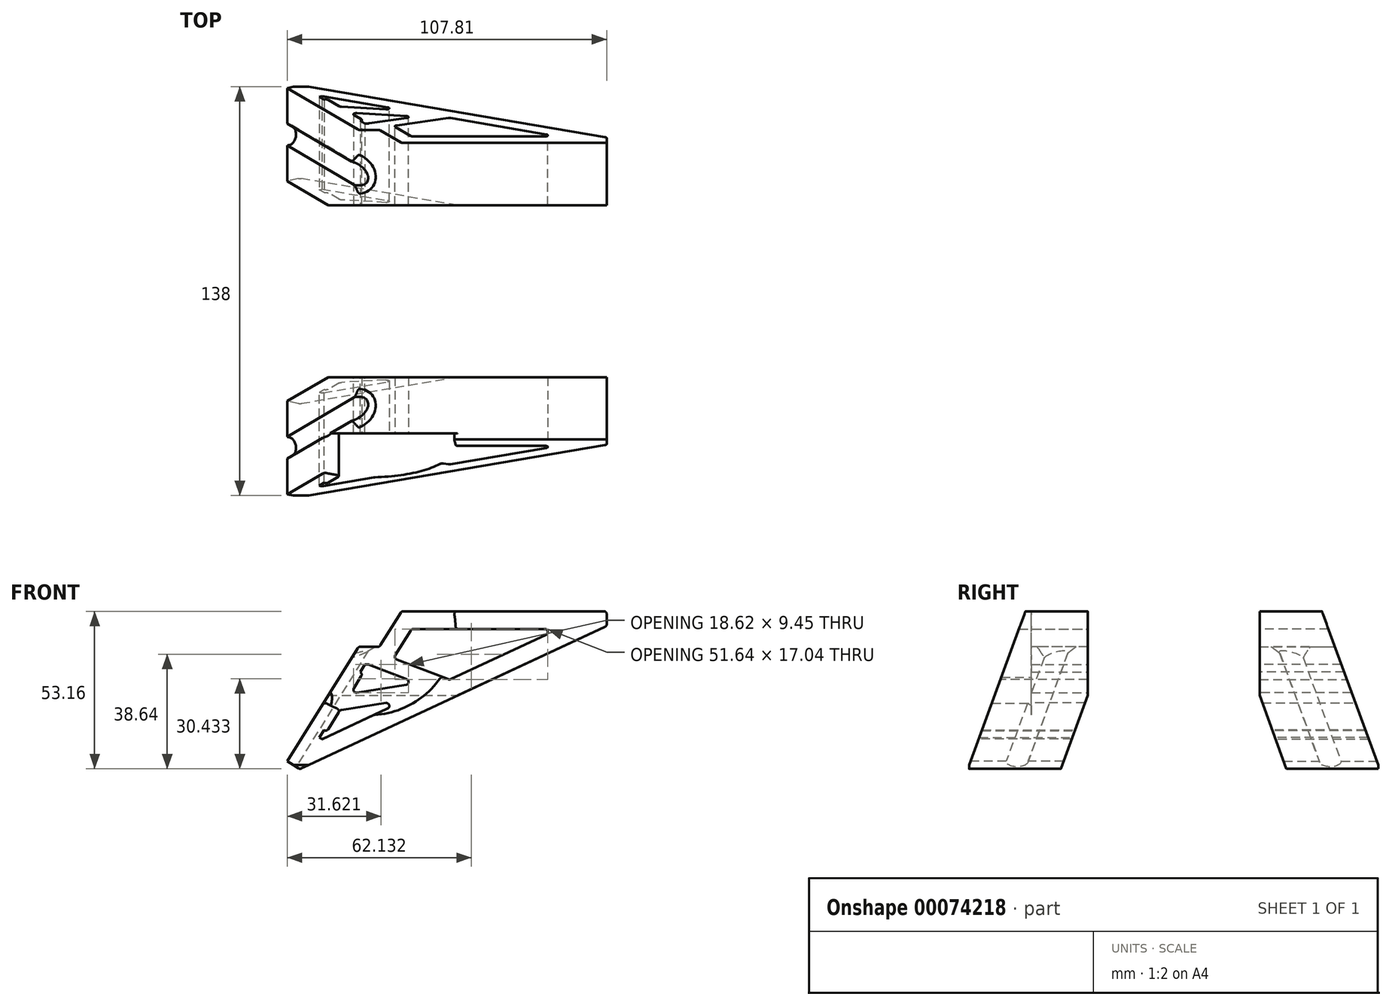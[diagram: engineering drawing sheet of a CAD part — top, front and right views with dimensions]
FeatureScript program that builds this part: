
annotation { "Feature Type Name" : "Feature", "Feature Type Description" : "" }
export const myFeature = defineFeature(function(context is Context, id is Id, definition is map)
    precondition{}
    {
        {
            var Q0;
            Q0=qCreatedBy(makeId("Front.planeOp"),FACE);
            cPlane(context, id + "F0", {"entities" : qUnion([Q0]), "cplaneType" : CPlaneType.OFFSET, "offset" : 88 * mm, "width" : 150 * mm, "height" : 150 * mm});
        }
        {
            var Q0;
            Q0=qCreatedBy(makeId("Front.planeOp"),FACE);
            var sketch = newSketch(context, id + "F1", { "sketchPlane" : qUnion([Q0])});
            skLineSegment(sketch, "E0", {"start": v(0, 0) * mm, "end": v(-100, 0) * mm});
            skLineSegment(sketch, "E1", {"start": v(-100, 0) * mm, "end": v(-151.66, -24.09) * mm});
            skLineSegment(sketch, "E2", {"start": v(-151.66, -24.09) * mm, "end": v(-166.46, -47.86) * mm});
            skSolve(sketch);
        }
        {
            var Q0;
            Q0=qCreatedBy(makeId("Right.planeOp"),FACE);
            var sketch = newSketch(context, id + "F2", { "sketchPlane" : qUnion([Q0])});
            skCircle(sketch, "E3", {"center": v(-4, 0) * mm, "radius": 4 * mm});
            skCircle(sketch, "E4", {"center": v(-84, 0) * mm, "radius": 4 * mm});
            skSolve(sketch);
        }
        {
            var Q0;
            Q0=qSketchRegion(id+"F2",true);
            var Q1;
            Q1=qConstructionFilter(qBodyType(qCreatedBy(id+"F1",EDGE),BodyType.WIRE),ConstructionObject.NO);
            sweep(context, id + "F3", {"profiles" : qUnion([Q0]), "path" : qUnion([Q1])});
        }
        {
            var Q0;
            Q0=qCreatedBy(makeId("Front.planeOp"),FACE);
            var Q1;
            Q1=qCreatedBy(id+"F0.planeOp",FACE);
            cPlane(context, id + "F4", {"entities" : qUnion([Q0, Q1]), "cplaneType" : CPlaneType.MID_PLANE, "offset" : 150 * mm, "width" : 150 * mm, "height" : 150 * mm});
        }
        {
            var Q0;
            Q0=qCreatedBy(id+"F4.planeOp",FACE);
            var sketch = newSketch(context, id + "F5", { "sketchPlane" : qUnion([Q0])});
            skCircle(sketch, "E5", {"center": v(0, 0) * mm, "radius": 5 * mm});
            skSolve(sketch);
        }
        {
            var Q0;
            Q0=makeQuery(id+"F3.opSweep","SWEPT_FACE",FACE,{"disambiguationData":[OSD([sQuery(id+"F1.wireOp",EDGE,"E2"),sQuery(id+"F2.wireOp",EDGE,"E3")])]});
            cPlane(context, id + "F6", {"entities" : qUnion([Q0]), "cplaneType" : CPlaneType.LINE_ANGLE, "offset" : 150 * mm, "angle" : 0 * degree, "width" : 150 * mm, "height" : 150 * mm});
        }
        {
            var Q0;
            Q0=qCreatedBy(id+"F6.planeOp",FACE);
            var Q1;
            Q1=sQuery(id+"F1.wireOp",VERTEX,"E0.start");
            cPlane(context, id + "F7", {"entities" : qUnion([Q0, Q1]), "cplaneType" : CPlaneType.PLANE_POINT, "offset" : 150 * mm, "width" : 150 * mm, "height" : 150 * mm});
        }
        {
            var Q0;
            Q0=qCreatedBy(id+"F7.planeOp",FACE);
            var sketch = newSketch(context, id + "F8", { "sketchPlane" : qUnion([Q0])});
            skLineSegment(sketch, "E6", {"start": v(80.5, 0) * mm, "end": v(119, -124) * mm});
            skLineSegment(sketch, "E7", {"start": v(119, -124) * mm, "end": v(119, -194) * mm});
            skLineSegment(sketch, "E8", {"start": v(80.5, 0) * mm, "end": v(44, 0) * mm});
            skSolve(sketch);
        }
        {
            var Q0;
            Q0=qCreatedBy(id+"F4.planeOp",FACE);
            var sketch = newSketch(context, id + "F9", { "sketchPlane" : qUnion([Q0])});
            skCircle(sketch, "E9", {"center": v(0, 0) * mm, "radius": 3.5 * mm});
            skSolve(sketch);
        }
        {
            var Q0;
            Q0=qSketchRegion(id+"F9",true);
            var Q1;
            Q1=qConstructionFilter(qBodyType(qCreatedBy(id+"F8",EDGE),BodyType.WIRE),ConstructionObject.NO);
            sweep(context, id + "F10", {"operationType" : NewBodyOperationType.ADD, "profiles" : qUnion([Q0]), "path" : qUnion([Q1])});
        }
        {
            var Q0;
            Q0=makeQuery(id+"F3.opSweep","SWEPT_BODY",BODY,{"disambiguationData":[OSD([sQuery(id+"F1.wireOp",EDGE,"E2"),sQuery(id+"F2.wireOp",EDGE,"E4")])]});
            var Q1;
            Q1=qCreatedBy(id+"F4.planeOp",FACE);
            mirror(context, id + "F11", {"operationType" : NewBodyOperationType.ADD, "entities" : qUnion([Q0]), "mirrorPlane" : qUnion([Q1])});
        }
        {
            var Q0;
            Q0=qSketchRegion(id+"F5",true);
            extrude(context, id + "F12", {"entities" : qUnion([Q0]), "operationType" : NewBodyOperationType.ADD, "depth" : 50 * mm, "hasSecondDirection" : true, "secondDirectionOppositeDirection" : true, "secondDirectionDepth" : 72 * mm});
        }
        {
            var Q0;
            Q0=makeQuery(id+"F12.opExtrude","CAP_FACE",FACE,{"disambiguationData":[OSD([sQuery(id+"F5.wireOp",EDGE,"E5")])],"isStart":false});
            var sketch = newSketch(context, id + "F13", { "sketchPlane" : qUnion([Q0])});
            skCircle(sketch, "E10", {"center": v(0, 0) * mm, "radius": 29 * mm});
            skSolve(sketch);
        }
        {
            var Q0;
            Q0 = qSketchRegion(id + "F13", true);
            extrude(context, id + "F14", {"entities" : qUnion([Q0]), "operationType" : NewBodyOperationType.ADD, "depth" : 25 * mm, "hasSecondDirection" : true, "secondDirectionOppositeDirection" : true, "secondDirectionDepth" : 2 * mm});
        }
        {
            var Q0;
            Q0=makeQuery(id+"F12.opExtrude","CAP_FACE",FACE,{"disambiguationData":[OSD([sQuery(id+"F5.wireOp",EDGE,"E5")])],"isStart":true});
            var sketch = newSketch(context, id + "F15", { "sketchPlane" : qUnion([Q0])});
            skCircle(sketch, "E11", {"center": v(0, 0) * mm, "radius": 27.5 * mm});
            skSolve(sketch);
        }
        {
            var Q0;
            Q0 = qSketchRegion(id + "F15", true);
            extrude(context, id + "F16", {"entities" : qUnion([Q0]), "operationType" : NewBodyOperationType.ADD, "depth" : 25 * mm});
        }
        {
            var Q0;
            Q0=qCreatedBy(makeId("Top.planeOp"),FACE);
            var sketch = newSketch(context, id + "F17", { "sketchPlane" : qUnion([Q0])});
            skCircle(sketch, "E12", {"center": v(0, -44) * mm, "radius": 2.5 * mm});
            skSolve(sketch);
        }
        {
            var Q0;
            Q0=qSketchRegion(id+"F17",true);
            extrude(context, id + "F18", {"entities" : qUnion([Q0]), "operationType" : NewBodyOperationType.REMOVE, "endBound" : BoundingType.THROUGH_ALL, "oppositeDirection" : true, "depth" : 25 * mm, "hasSecondDirection" : true, "secondDirectionBound" : SecondDirectionBoundingType.THROUGH_ALL, "secondDirectionOppositeDirection" : false, "secondDirectionDepth" : 25 * mm});
        }
        {
            var Q0;
            Q0=qCreatedBy(makeId("Front.planeOp"),FACE);
            var sketch = newSketch(context, id + "F19", { "sketchPlane" : qUnion([Q0])});
            skLineSegment(sketch, "E13", {"start": v(3.33, -6) * mm, "end": v(10.8, 6) * mm});
            skLineSegment(sketch, "E14", {"start": v(10.8, 6) * mm, "end": v(80, 6) * mm});
            skLineSegment(sketch, "E15", {"start": v(80, 6) * mm, "end": v(80, 1) * mm});
            skLineSegment(sketch, "E16", {"start": v(80, 1) * mm, "end": v(-23.56, -47.3) * mm});
            skLineSegment(sketch, "E17", {"start": v(-23.56, -47.3) * mm, "end": v(-27.8, -44.65) * mm});
            skLineSegment(sketch, "E18", {"start": v(-27.8, -44.65) * mm, "end": v(-3.74, -6) * mm});
            skLineSegment(sketch, "E19", {"start": v(-3.74, -6) * mm, "end": v(3.33, -6) * mm});
            skSolve(sketch);
        }
        {
            var Q0;
            Q0 = qSketchRegion(id + "F19", true);
            extrude(context, id + "F20", {"entities" : qUnion([Q0]), "depth" : 15 * mm, "hasSecondDirection" : true, "secondDirectionOppositeDirection" : true, "secondDirectionDepth" : 25 * mm});
        }
        {
            var Q0;
            Q0=qCreatedBy(makeId("Front.planeOp"),FACE);
            var sketch = newSketch(context, id + "F21", { "sketchPlane" : qUnion([Q0])});
            skLineSegment(sketch, "E20.0", {"start": v(63.66, 0) * mm, "end": v(26.93, -17.13) * mm});
            skLineSegment(sketch, "E20.1", {"start": v(14.14, 0) * mm, "end": v(63.66, 0) * mm});
            skLineSegment(sketch, "E20.2", {"start": v(-14.5, -34.64) * mm, "end": v(-10, -27.4) * mm});
            skLineSegment(sketch, "E20.3", {"start": v(-0.4, -12) * mm, "end": v(-0.3, -12) * mm});
            skLineSegment(sketch, "E20.4", {"start": v(8, -9.84) * mm, "end": v(14.14, 0) * mm});
            skLineSegment(sketch, "E21", {"start": v(23.78, -18.6) * mm, "end": v(6.66, -12) * mm, "construction": true});
            skLineSegment(sketch, "E22", {"start": v(15.97, -18.26) * mm, "end": v(-0.3, -12) * mm});
            skLineSegment(sketch, "E23", {"start": v(26.93, -17.13) * mm, "end": v(8, -9.84) * mm});
            skLineSegment(sketch, "E24.trimOffspring", {"start": v(12.46, -23.88) * mm, "end": v(-16.1, -37.19) * mm});
            skLineSegment(sketch, "E25", {"start": v(-8.25, -24.6) * mm, "end": v(20.64, -20.06) * mm, "construction": true});
            skLineSegment(sketch, "E26", {"start": v(-6.5, -21.79) * mm, "end": v(15.97, -18.26) * mm});
            skLineSegment(sketch, "E27", {"start": v(-10, -27.4) * mm, "end": v(12.46, -23.88) * mm});
            skLineSegment(sketch, "E28.trimOffspring", {"start": v(-6.5, -21.79) * mm, "end": v(-2.32, -15.08) * mm});
            skLineSegment(sketch, "E29", {"start": v(-0.4, -12) * mm, "end": v(-1.58, -12) * mm});
            skLineSegment(sketch, "E30", {"start": v(-1.58, -12) * mm, "end": v(-3.17, -14.55) * mm});
            skLineSegment(sketch, "E31", {"start": v(-3.17, -14.55) * mm, "end": v(-2.32, -15.08) * mm});
            skLineSegment(sketch, "E32", {"start": v(-16.1, -37.19) * mm, "end": v(-16.94, -36.66) * mm});
            skLineSegment(sketch, "E33", {"start": v(-16.94, -36.66) * mm, "end": v(-15.35, -34.11) * mm});
            skLineSegment(sketch, "E34", {"start": v(-15.35, -34.11) * mm, "end": v(-14.5, -34.64) * mm});
            skSolve(sketch);
        }
        {
            var Q0;
            Q0 = qSketchRegion(id + "F21", true);
            extrude(context, id + "F22", {"entities" : qUnion([Q0]), "operationType" : NewBodyOperationType.REMOVE, "endBound" : BoundingType.THROUGH_ALL, "oppositeDirection" : true, "depth" : 25 * mm, "hasSecondDirection" : true, "secondDirectionBound" : SecondDirectionBoundingType.THROUGH_ALL, "secondDirectionOppositeDirection" : false, "secondDirectionDepth" : 25 * mm});
        }
        {
            var Q0;
            Q0=qCreatedBy(id+"F7.planeOp",FACE);
            var sketch = newSketch(context, id + "F23", { "sketchPlane" : qUnion([Q0])});
            skLineSegment(sketch, "E35.0", {"start": v(80.5, 0) * mm, "end": v(44, 0) * mm, "construction": true});
            skLineSegment(sketch, "E36.0", {"start": v(80.5, 0) * mm, "end": v(119, -124) * mm, "construction": true});
            skLineSegment(sketch, "E37.0", {"start": v(119, -124) * mm, "end": v(119, -194) * mm, "construction": true});
            skLineSegment(sketch, "E38.MirrorCS", {"start": v(7.5, 0) * mm, "end": v(-31, -124) * mm, "construction": true});
            skLineSegment(sketch, "E39.MirrorCS", {"start": v(-31, -124) * mm, "end": v(-31, -194) * mm, "construction": true});
            skLineSegment(sketch, "E40.MirrorCS", {"start": v(7.5, 0) * mm, "end": v(44, 0) * mm, "construction": true});
            skLineSegment(sketch, "E41.0", {"start": v(104, -126.28) * mm, "end": v(104, -194) * mm, "construction": true});
            skLineSegment(sketch, "E41.1", {"start": v(69.45, -15) * mm, "end": v(104, -126.28) * mm, "construction": true});
            skLineSegment(sketch, "E41.2", {"start": v(-16, -126.28) * mm, "end": v(-16, -194) * mm, "construction": true});
            skLineSegment(sketch, "E41.3", {"start": v(18.55, -15) * mm, "end": v(-16, -126.28) * mm});
            skLineSegment(sketch, "E41.4", {"start": v(18.55, -15) * mm, "end": v(44, -15) * mm, "construction": true});
            skLineSegment(sketch, "E41.5", {"start": v(69.45, -15) * mm, "end": v(44, -15) * mm, "construction": true});
            skLineSegment(sketch, "E42.0", {"start": v(-46, -121.72) * mm, "end": v(-46, -194) * mm, "construction": true});
            skLineSegment(sketch, "E42.1", {"start": v(-3.55, 15) * mm, "end": v(-46, -121.72) * mm});
            skLineSegment(sketch, "E42.2", {"start": v(134, -121.72) * mm, "end": v(134, -194) * mm, "construction": true});
            skLineSegment(sketch, "E42.3", {"start": v(91.55, 15) * mm, "end": v(134, -121.72) * mm, "construction": true});
            skLineSegment(sketch, "E42.4", {"start": v(91.55, 15) * mm, "end": v(44, 15) * mm, "construction": true});
            skLineSegment(sketch, "E42.5", {"start": v(-3.55, 15) * mm, "end": v(44, 15) * mm, "construction": true});
            skLineSegment(sketch, "E43", {"start": v(-3.55, 15) * mm, "end": v(-46, 15) * mm});
            skLineSegment(sketch, "E44", {"start": v(-46, 15) * mm, "end": v(-46, -121.72) * mm});
            skLineSegment(sketch, "E45", {"start": v(-16, -126.28) * mm, "end": v(18.55, -126.28) * mm});
            skLineSegment(sketch, "E46", {"start": v(18.55, -126.28) * mm, "end": v(18.55, -15) * mm});
            skSolve(sketch);
        }
        {
            var Q0;
            Q0=qCreatedBy(makeId("Right.planeOp"),FACE);
            var sketch = newSketch(context, id + "F24", { "sketchPlane" : qUnion([Q0])});
            skLineSegment(sketch, "E47.0", {"start": v(3.55, 12.73) * mm, "end": v(46, 12.73) * mm});
            skLineSegment(sketch, "E48.0", {"start": v(3.55, 12.73) * mm, "end": v(46, -103.33) * mm});
            skLineSegment(sketch, "E49.0", {"start": v(46, 12.73) * mm, "end": v(46, -103.33) * mm});
            skLineSegment(sketch, "E50.0", {"start": v(-18.55, -107.19) * mm, "end": v(-18.55, -12.73) * mm});
            skLineSegment(sketch, "E51.0", {"start": v(16, -107.19) * mm, "end": v(-18.55, -107.19) * mm});
            skLineSegment(sketch, "E52.0", {"start": v(-18.55, -12.73) * mm, "end": v(16, -107.19) * mm});
            skSolve(sketch);
        }
        {
            var Q0;
            Q0 = qSketchRegion(id + "F24", true);
            extrude(context, id + "F25", {"entities" : qUnion([Q0]), "operationType" : NewBodyOperationType.REMOVE, "endBound" : BoundingType.THROUGH_ALL, "oppositeDirection" : true, "depth" : 25 * mm, "hasSecondDirection" : true, "secondDirectionBound" : SecondDirectionBoundingType.THROUGH_ALL, "secondDirectionOppositeDirection" : false, "secondDirectionDepth" : 25 * mm});
        }
        {
            var Q0;
            Q0=makeQuery(id+"F20.opExtrude","SWEPT_BODY",BODY,{"disambiguationData":[OSD([sQuery(id+"F19.wireOp",EDGE,"E13"),sQuery(id+"F19.wireOp",EDGE,"E14"),sQuery(id+"F19.wireOp",EDGE,"E15"),sQuery(id+"F19.wireOp",EDGE,"E16"),sQuery(id+"F19.wireOp",EDGE,"E17"),sQuery(id+"F19.wireOp",EDGE,"E18"),sQuery(id+"F19.wireOp",EDGE,"E19")])]});
            var Q1;
            Q1=qCreatedBy(id+"F4.planeOp",FACE);
            mirror(context, id + "F26", {"entities" : qUnion([Q0]), "mirrorPlane" : qUnion([Q1])});
        }
        {
            var Q0;
            Q0=makeQuery(id+"F3.opSweep","SWEPT_BODY",BODY,{"disambiguationData":[OSD([sQuery(id+"F1.wireOp",EDGE,"E2"),sQuery(id+"F2.wireOp",EDGE,"E3")])]});
            var Q1;
            Q1=makeQuery(id+"F20.opExtrude","SWEPT_BODY",BODY,{"disambiguationData":[OSD([sQuery(id+"F19.wireOp",EDGE,"E13"),sQuery(id+"F19.wireOp",EDGE,"E14"),sQuery(id+"F19.wireOp",EDGE,"E15"),sQuery(id+"F19.wireOp",EDGE,"E16"),sQuery(id+"F19.wireOp",EDGE,"E17"),sQuery(id+"F19.wireOp",EDGE,"E18"),sQuery(id+"F19.wireOp",EDGE,"E19")])]});
            var Q2;
            Q2=makeQuery(id+"F26.opPattern","COPY",BODY,{"derivedFrom":makeQuery(id+"F20.opExtrude","SWEPT_BODY",BODY,{"disambiguationData":[OSD([sQuery(id+"F19.wireOp",EDGE,"E13"),sQuery(id+"F19.wireOp",EDGE,"E14"),sQuery(id+"F19.wireOp",EDGE,"E15"),sQuery(id+"F19.wireOp",EDGE,"E16"),sQuery(id+"F19.wireOp",EDGE,"E17"),sQuery(id+"F19.wireOp",EDGE,"E18"),sQuery(id+"F19.wireOp",EDGE,"E19")])]}),"instanceName":"1"});
            booleanBodies(context, id + "F27", {"operationType" : BooleanOperationType.SUBTRACTION, "tools" : qUnion([Q0]), "targets" : qUnion([Q1, Q2])});
        }
        {
            var Q0;
            Q0=makeQuery(id+"F27.opBoolean","INTERSECT",EDGE,{"derivedFrom":[makeQuery(id+"F11.opPattern","COPY",FACE,{"derivedFrom":makeQuery(id+"F10.opSweep","SWEPT_FACE",FACE,{"disambiguationData":[OSD([sQuery(id+"F8.wireOp",EDGE,"E6"),sQuery(id+"F9.wireOp",EDGE,"E9")])]}),"instanceName":"1"}),makeQuery(id+"F20.opExtrude","SWEPT_FACE",FACE,{"disambiguationData":[OSD([sQuery(id+"F19.wireOp",EDGE,"E19")])]})]});
            var Q1;
            Q1=makeQuery(id+"F27.opBoolean","INTERSECT",EDGE,{"derivedFrom":[makeQuery(id+"F10.opSweep","SWEPT_FACE",FACE,{"disambiguationData":[OSD([sQuery(id+"F8.wireOp",EDGE,"E6"),sQuery(id+"F9.wireOp",EDGE,"E9")])]}),makeQuery(id+"F26.opPattern","COPY",FACE,{"derivedFrom":makeQuery(id+"F20.opExtrude","SWEPT_FACE",FACE,{"disambiguationData":[OSD([sQuery(id+"F19.wireOp",EDGE,"E19")])]}),"instanceName":"1"})]});
            chamfer(context, id + "F28", {"entities" : qUnion([Q0, Q1]), "width" : 3 * mm, "tangentPropagation" : true});
        }
        {
            var Q0;
            Q0=makeQuery(id+"F22.boolean.opBoolean","COPY",EDGE,{"derivedFrom":makeQuery(id+"F22.opExtrude","SWEPT_EDGE",EDGE,{"disambiguationData":[OSD([sQuery(id+"F21.wireOp",EDGE,"E20.0"),sQuery(id+"F21.wireOp",EDGE,"E20.1")])]})});
            var Q1;
            Q1=makeQuery(id+"F22.boolean.opBoolean","COPY",EDGE,{"derivedFrom":makeQuery(id+"F22.opExtrude","SWEPT_EDGE",EDGE,{"disambiguationData":[OSD([sQuery(id+"F21.wireOp",EDGE,"E20.1"),sQuery(id+"F21.wireOp",EDGE,"E20.4")])]})});
            var Q2;
            Q2=makeQuery(id+"F22.boolean.opBoolean","COPY",EDGE,{"derivedFrom":makeQuery(id+"F22.opExtrude","SWEPT_EDGE",EDGE,{"disambiguationData":[OSD([sQuery(id+"F21.wireOp",EDGE,"E20.4"),sQuery(id+"F21.wireOp",EDGE,"E23")])]})});
            var Q3;
            Q3=makeQuery(id+"F22.boolean.opBoolean","COPY",EDGE,{"derivedFrom":makeQuery(id+"F22.opExtrude","SWEPT_EDGE",EDGE,{"disambiguationData":[OSD([sQuery(id+"F21.wireOp",EDGE,"E20.0"),sQuery(id+"F21.wireOp",EDGE,"E23")])]})});
            var Q4;
            Q4=makeQuery(id+"F22.boolean.opBoolean","COPY",EDGE,{"derivedFrom":makeQuery(id+"F22.opExtrude","SWEPT_EDGE",EDGE,{"disambiguationData":[OSD([sQuery(id+"F21.wireOp",EDGE,"E22"),sQuery(id+"F21.wireOp",EDGE,"E26")])]})});
            var Q5;
            Q5=makeQuery(id+"F22.boolean.opBoolean","COPY",EDGE,{"derivedFrom":makeQuery(id+"F22.opExtrude","SWEPT_EDGE",EDGE,{"disambiguationData":[OSD([sQuery(id+"F21.wireOp",EDGE,"E26"),sQuery(id+"F21.wireOp",EDGE,"E28.trimOffspring")])]})});
            var Q6;
            Q6=makeQuery(id+"F22.boolean.opBoolean","COPY",EDGE,{"derivedFrom":makeQuery(id+"F22.opExtrude","SWEPT_EDGE",EDGE,{"disambiguationData":[OSD([sQuery(id+"F21.wireOp",EDGE,"E20.2"),sQuery(id+"F21.wireOp",EDGE,"E27")])]})});
            var Q7;
            Q7=makeQuery(id+"F22.boolean.opBoolean","COPY",EDGE,{"derivedFrom":makeQuery(id+"F22.opExtrude","SWEPT_EDGE",EDGE,{"disambiguationData":[OSD([sQuery(id+"F21.wireOp",EDGE,"E24.trimOffspring"),sQuery(id+"F21.wireOp",EDGE,"E27")])]})});
            var Q8;
            Q8=makeQuery(id+"F20.opExtrude","SWEPT_EDGE",EDGE,{"disambiguationData":[OSD([sQuery(id+"F19.wireOp",EDGE,"E13"),sQuery(id+"F19.wireOp",EDGE,"E19")])]});
            var Q9;
            Q9=makeQuery(id+"F22.boolean.opBoolean","COPY",EDGE,{"derivedFrom":makeQuery(id+"F22.opExtrude","SWEPT_EDGE",EDGE,{"disambiguationData":[OSD([sQuery(id+"F21.wireOp",EDGE,"E20.3"),sQuery(id+"F21.wireOp",EDGE,"E22")])]})});
            var Q10;
            Q10=makeQuery(id+"F22.boolean.opBoolean","COPY",EDGE,{"derivedFrom":makeQuery(id+"F22.opExtrude","SWEPT_EDGE",EDGE,{"disambiguationData":[OSD([sQuery(id+"F21.wireOp",EDGE,"E28.trimOffspring"),sQuery(id+"F21.wireOp",EDGE,"E31")])]})});
            var Q11;
            Q11=makeQuery(id+"F22.boolean.opBoolean","COPY",EDGE,{"derivedFrom":makeQuery(id+"F22.opExtrude","SWEPT_EDGE",EDGE,{"disambiguationData":[OSD([sQuery(id+"F21.wireOp",EDGE,"E20.2"),sQuery(id+"F21.wireOp",EDGE,"E34")])]})});
            var Q12;
            Q12=makeQuery(id+"F20.opExtrude","SWEPT_EDGE",EDGE,{"disambiguationData":[OSD([sQuery(id+"F19.wireOp",EDGE,"E14"),sQuery(id+"F19.wireOp",EDGE,"E15")])]});
            var Q13;
            Q13=makeQuery(id+"F20.opExtrude","SWEPT_EDGE",EDGE,{"disambiguationData":[OSD([sQuery(id+"F19.wireOp",EDGE,"E15"),sQuery(id+"F19.wireOp",EDGE,"E16")])]});
            var Q14;
            Q14=makeQuery(id+"F20.opExtrude","SWEPT_EDGE",EDGE,{"disambiguationData":[OSD([sQuery(id+"F19.wireOp",EDGE,"E16"),sQuery(id+"F19.wireOp",EDGE,"E17")])]});
            var Q15;
            Q15=makeQuery(id+"F20.opExtrude","SWEPT_EDGE",EDGE,{"disambiguationData":[OSD([sQuery(id+"F19.wireOp",EDGE,"E13"),sQuery(id+"F19.wireOp",EDGE,"E14")])]});
            var Q16;
            {var subQ0=sQuery(id+"F19.wireOp",EDGE,"E19");var subQ1=sQuery(id+"F19.wireOp",EDGE,"E18");Q16=makeQuery(id+"F27.opBoolean","SPLIT",EDGE,{"disambiguationData":[TD([makeQuery(id+"F20.opExtrude","CAP_FACE",FACE,{"disambiguationData":[OSD([sQuery(id+"F19.wireOp",EDGE,"E13"),sQuery(id+"F19.wireOp",EDGE,"E14"),sQuery(id+"F19.wireOp",EDGE,"E15"),sQuery(id+"F19.wireOp",EDGE,"E16"),sQuery(id+"F19.wireOp",EDGE,"E17"),subQ1,subQ0])],"isStart":false})])],"derivedFrom":makeQuery(id+"F20.opExtrude","SWEPT_EDGE",EDGE,{"disambiguationData":[OSD([subQ1,subQ0])]})});}
            var Q17;
            {var subQ0=sQuery(id+"F19.wireOp",EDGE,"E18");var subQ1=sQuery(id+"F19.wireOp",EDGE,"E19");Q17=makeQuery(id+"F27.opBoolean","SPLIT",EDGE,{"disambiguationData":[TD([makeQuery(id+"F25.boolean.opBoolean","COPY",FACE,{"derivedFrom":makeQuery(id+"F25.opExtrude","SWEPT_FACE",FACE,{"disambiguationData":[OSD([sQuery(id+"F24.wireOp",EDGE,"E48.0")])]})})])],"derivedFrom":makeQuery(id+"F20.opExtrude","SWEPT_EDGE",EDGE,{"disambiguationData":[OSD([subQ0,subQ1])]})});}
            var Q18;
            Q18=makeQuery(id+"F26.opPattern","COPY",EDGE,{"derivedFrom":makeQuery(id+"F20.opExtrude","SWEPT_EDGE",EDGE,{"disambiguationData":[OSD([sQuery(id+"F19.wireOp",EDGE,"E13"),sQuery(id+"F19.wireOp",EDGE,"E14")])]}),"instanceName":"1"});
            var Q19;
            Q19=makeQuery(id+"F26.opPattern","COPY",EDGE,{"derivedFrom":makeQuery(id+"F20.opExtrude","SWEPT_EDGE",EDGE,{"disambiguationData":[OSD([sQuery(id+"F19.wireOp",EDGE,"E14"),sQuery(id+"F19.wireOp",EDGE,"E15")])]}),"instanceName":"1"});
            var Q20;
            Q20=makeQuery(id+"F26.opPattern","COPY",EDGE,{"derivedFrom":makeQuery(id+"F22.boolean.opBoolean","COPY",EDGE,{"derivedFrom":makeQuery(id+"F22.opExtrude","SWEPT_EDGE",EDGE,{"disambiguationData":[OSD([sQuery(id+"F21.wireOp",EDGE,"E24.trimOffspring"),sQuery(id+"F21.wireOp",EDGE,"E27")])]})}),"instanceName":"1"});
            var Q21;
            Q21=makeQuery(id+"F26.opPattern","COPY",EDGE,{"derivedFrom":makeQuery(id+"F22.boolean.opBoolean","COPY",EDGE,{"derivedFrom":makeQuery(id+"F22.opExtrude","SWEPT_EDGE",EDGE,{"disambiguationData":[OSD([sQuery(id+"F21.wireOp",EDGE,"E22"),sQuery(id+"F21.wireOp",EDGE,"E26")])]})}),"instanceName":"1"});
            var Q22;
            {var subQ0=sQuery(id+"F19.wireOp",EDGE,"E18");var subQ1=sQuery(id+"F19.wireOp",EDGE,"E19");Q22=makeQuery(id+"F27.opBoolean","SPLIT",EDGE,{"disambiguationData":[TD([makeQuery(id+"F14.opExtrude","CAP_FACE",FACE,{"disambiguationData":[OSD([sQuery(id+"F13.wireOp",EDGE,"E10")])],"isStart":true})])],"derivedFrom":makeQuery(id+"F26.opPattern","COPY",EDGE,{"derivedFrom":makeQuery(id+"F20.opExtrude","SWEPT_EDGE",EDGE,{"disambiguationData":[OSD([subQ0,subQ1])]}),"instanceName":"1"})});}
            var Q23;
            Q23=makeQuery(id+"F26.opPattern","COPY",EDGE,{"derivedFrom":makeQuery(id+"F20.opExtrude","SWEPT_EDGE",EDGE,{"disambiguationData":[OSD([sQuery(id+"F19.wireOp",EDGE,"E13"),sQuery(id+"F19.wireOp",EDGE,"E19")])]}),"instanceName":"1"});
            var Q24;
            {var subQ0=sQuery(id+"F19.wireOp",EDGE,"E18");var subQ1=sQuery(id+"F19.wireOp",EDGE,"E19");Q24=makeQuery(id+"F27.opBoolean","SPLIT",EDGE,{"disambiguationData":[TD([makeQuery(id+"F26.opPattern","COPY",FACE,{"derivedFrom":makeQuery(id+"F20.opExtrude","CAP_FACE",FACE,{"disambiguationData":[OSD([sQuery(id+"F19.wireOp",EDGE,"E13"),sQuery(id+"F19.wireOp",EDGE,"E14"),sQuery(id+"F19.wireOp",EDGE,"E15"),sQuery(id+"F19.wireOp",EDGE,"E16"),sQuery(id+"F19.wireOp",EDGE,"E17"),subQ0,subQ1])],"isStart":false}),"instanceName":"1"})])],"derivedFrom":makeQuery(id+"F26.opPattern","COPY",EDGE,{"derivedFrom":makeQuery(id+"F20.opExtrude","SWEPT_EDGE",EDGE,{"disambiguationData":[OSD([subQ0,subQ1])]}),"instanceName":"1"})});}
            var Q25;
            Q25=makeQuery(id+"F26.opPattern","COPY",EDGE,{"derivedFrom":makeQuery(id+"F20.opExtrude","SWEPT_EDGE",EDGE,{"disambiguationData":[OSD([sQuery(id+"F19.wireOp",EDGE,"E16"),sQuery(id+"F19.wireOp",EDGE,"E17")])]}),"instanceName":"1"});
            var Q26;
            Q26=makeQuery(id+"F26.opPattern","COPY",EDGE,{"derivedFrom":makeQuery(id+"F20.opExtrude","SWEPT_EDGE",EDGE,{"disambiguationData":[OSD([sQuery(id+"F19.wireOp",EDGE,"E15"),sQuery(id+"F19.wireOp",EDGE,"E16")])]}),"instanceName":"1"});
            var Q27;
            Q27=makeQuery(id+"F26.opPattern","COPY",EDGE,{"derivedFrom":makeQuery(id+"F22.boolean.opBoolean","COPY",EDGE,{"derivedFrom":makeQuery(id+"F22.opExtrude","SWEPT_EDGE",EDGE,{"disambiguationData":[OSD([sQuery(id+"F21.wireOp",EDGE,"E20.1"),sQuery(id+"F21.wireOp",EDGE,"E20.4")])]})}),"instanceName":"1"});
            var Q28;
            Q28=makeQuery(id+"F26.opPattern","COPY",EDGE,{"derivedFrom":makeQuery(id+"F22.boolean.opBoolean","COPY",EDGE,{"derivedFrom":makeQuery(id+"F22.opExtrude","SWEPT_EDGE",EDGE,{"disambiguationData":[OSD([sQuery(id+"F21.wireOp",EDGE,"E20.0"),sQuery(id+"F21.wireOp",EDGE,"E20.1")])]})}),"instanceName":"1"});
            var Q29;
            Q29=makeQuery(id+"F26.opPattern","COPY",EDGE,{"derivedFrom":makeQuery(id+"F22.boolean.opBoolean","COPY",EDGE,{"derivedFrom":makeQuery(id+"F22.opExtrude","SWEPT_EDGE",EDGE,{"disambiguationData":[OSD([sQuery(id+"F21.wireOp",EDGE,"E20.0"),sQuery(id+"F21.wireOp",EDGE,"E23")])]})}),"instanceName":"1"});
            var Q30;
            Q30=makeQuery(id+"F26.opPattern","COPY",EDGE,{"derivedFrom":makeQuery(id+"F22.boolean.opBoolean","COPY",EDGE,{"derivedFrom":makeQuery(id+"F22.opExtrude","SWEPT_EDGE",EDGE,{"disambiguationData":[OSD([sQuery(id+"F21.wireOp",EDGE,"E20.4"),sQuery(id+"F21.wireOp",EDGE,"E23")])]})}),"instanceName":"1"});
            var Q31;
            Q31=makeQuery(id+"F26.opPattern","COPY",EDGE,{"derivedFrom":makeQuery(id+"F22.boolean.opBoolean","COPY",EDGE,{"derivedFrom":makeQuery(id+"F22.opExtrude","SWEPT_EDGE",EDGE,{"disambiguationData":[OSD([sQuery(id+"F21.wireOp",EDGE,"E26"),sQuery(id+"F21.wireOp",EDGE,"E28.trimOffspring")])]})}),"instanceName":"1"});
            var Q32;
            Q32=makeQuery(id+"F26.opPattern","COPY",EDGE,{"derivedFrom":makeQuery(id+"F22.boolean.opBoolean","COPY",EDGE,{"derivedFrom":makeQuery(id+"F22.opExtrude","SWEPT_EDGE",EDGE,{"disambiguationData":[OSD([sQuery(id+"F21.wireOp",EDGE,"E20.3"),sQuery(id+"F21.wireOp",EDGE,"E22")])]})}),"instanceName":"1"});
            var Q33;
            Q33=makeQuery(id+"F26.opPattern","COPY",EDGE,{"derivedFrom":makeQuery(id+"F22.boolean.opBoolean","COPY",EDGE,{"derivedFrom":makeQuery(id+"F22.opExtrude","SWEPT_EDGE",EDGE,{"disambiguationData":[OSD([sQuery(id+"F21.wireOp",EDGE,"E20.2"),sQuery(id+"F21.wireOp",EDGE,"E27")])]})}),"instanceName":"1"});
            var Q34;
            Q34=makeQuery(id+"F26.opPattern","COPY",EDGE,{"derivedFrom":makeQuery(id+"F22.boolean.opBoolean","COPY",EDGE,{"derivedFrom":makeQuery(id+"F22.opExtrude","SWEPT_EDGE",EDGE,{"disambiguationData":[OSD([sQuery(id+"F21.wireOp",EDGE,"E24.trimOffspring"),sQuery(id+"F21.wireOp",EDGE,"E32")])]})}),"instanceName":"1"});
            var Q35;
            Q35=makeQuery(id+"F26.opPattern","COPY",EDGE,{"derivedFrom":makeQuery(id+"F22.boolean.opBoolean","COPY",EDGE,{"derivedFrom":makeQuery(id+"F22.opExtrude","SWEPT_EDGE",EDGE,{"disambiguationData":[OSD([sQuery(id+"F21.wireOp",EDGE,"E20.2"),sQuery(id+"F21.wireOp",EDGE,"E34")])]})}),"instanceName":"1"});
            var Q36;
            Q36=makeQuery(id+"F26.opPattern","COPY",EDGE,{"derivedFrom":makeQuery(id+"F22.boolean.opBoolean","COPY",EDGE,{"derivedFrom":makeQuery(id+"F22.opExtrude","SWEPT_EDGE",EDGE,{"disambiguationData":[OSD([sQuery(id+"F21.wireOp",EDGE,"E28.trimOffspring"),sQuery(id+"F21.wireOp",EDGE,"E31")])]})}),"instanceName":"1"});
            var Q37;
            Q37=makeQuery(id+"F27.opBoolean","INTERSECT",EDGE,{"derivedFrom":[makeQuery(id+"F14.opExtrude","SWEPT_FACE",FACE,{"disambiguationData":[OSD([sQuery(id+"F13.wireOp",EDGE,"E10")])]}),makeQuery(id+"F26.opPattern","COPY",FACE,{"derivedFrom":makeQuery(id+"F22.boolean.opBoolean","COPY",FACE,{"derivedFrom":makeQuery(id+"F22.opExtrude","SWEPT_FACE",FACE,{"disambiguationData":[OSD([sQuery(id+"F21.wireOp",EDGE,"E23")])]})}),"instanceName":"1"})]});
            var Q38;
            Q38=makeQuery(id+"F27.opBoolean","INTERSECT",EDGE,{"derivedFrom":[makeQuery(id+"F14.opExtrude","SWEPT_FACE",FACE,{"disambiguationData":[OSD([sQuery(id+"F13.wireOp",EDGE,"E10")])]}),makeQuery(id+"F26.opPattern","COPY",FACE,{"derivedFrom":makeQuery(id+"F22.boolean.opBoolean","COPY",FACE,{"derivedFrom":makeQuery(id+"F22.opExtrude","SWEPT_FACE",FACE,{"disambiguationData":[OSD([sQuery(id+"F21.wireOp",EDGE,"E24.trimOffspring")])]})}),"instanceName":"1"})]});
            var Q39;
            Q39=makeQuery(id+"F27.opBoolean","INTERSECT",EDGE,{"derivedFrom":[makeQuery(id+"F14.opExtrude","SWEPT_FACE",FACE,{"disambiguationData":[OSD([sQuery(id+"F13.wireOp",EDGE,"E10")])]}),makeQuery(id+"F26.opPattern","COPY",FACE,{"derivedFrom":makeQuery(id+"F20.opExtrude","SWEPT_FACE",FACE,{"disambiguationData":[OSD([sQuery(id+"F19.wireOp",EDGE,"E18")])]}),"instanceName":"1"})]});
            var Q40;
            Q40=makeQuery(id+"F27.opBoolean","INTERSECT",EDGE,{"derivedFrom":[makeQuery(id+"F14.opExtrude","SWEPT_FACE",FACE,{"disambiguationData":[OSD([sQuery(id+"F13.wireOp",EDGE,"E10")])]}),makeQuery(id+"F26.opPattern","COPY",FACE,{"derivedFrom":makeQuery(id+"F22.boolean.opBoolean","COPY",FACE,{"derivedFrom":makeQuery(id+"F22.opExtrude","SWEPT_FACE",FACE,{"disambiguationData":[OSD([sQuery(id+"F21.wireOp",EDGE,"E20.1")])]})}),"instanceName":"1"})]});
            var Q41;
            Q41=makeQuery(id+"F27.opBoolean","INTERSECT",EDGE,{"derivedFrom":[makeQuery(id+"F14.opExtrude","SWEPT_FACE",FACE,{"disambiguationData":[OSD([sQuery(id+"F13.wireOp",EDGE,"E10")])]}),makeQuery(id+"F26.opPattern","COPY",FACE,{"derivedFrom":makeQuery(id+"F20.opExtrude","SWEPT_FACE",FACE,{"disambiguationData":[OSD([sQuery(id+"F19.wireOp",EDGE,"E14")])]}),"instanceName":"1"})]});
            fillet(context, id + "F29", {"entities" : qUnion([Q0, Q1, Q2, Q3, Q4, Q5, Q6, Q7, Q8, Q9, Q10, Q11, Q12, Q13, Q14, Q15, Q16, Q17, Q18, Q19, Q20, Q21, Q22, Q23, Q24, Q25, Q26, Q27, Q28, Q29, Q30, Q31, Q32, Q33, Q34, Q35, Q36, Q37, Q38, Q39, Q40, Q41]), "radius" : 1 * mm, "tangentPropagation" : true, "allowEdgeOverflow" : false});
        }
        {
            var Q0;
            Q0=makeQuery(id+"F29.opFillet","BLEND_EDGE",EDGE,{"blendedFrom":[makeQuery(id+"F26.opPattern","COPY",EDGE,{"derivedFrom":makeQuery(id+"F22.boolean.opBoolean","COPY",EDGE,{"derivedFrom":makeQuery(id+"F22.opExtrude","SWEPT_EDGE",EDGE,{"disambiguationData":[OSD([sQuery(id+"F21.wireOp",EDGE,"E20.2"),sQuery(id+"F21.wireOp",EDGE,"E27")])]})}),"instanceName":"1"}),makeQuery(id+"F27.opBoolean","COPY",FACE,{"disambiguationData":[OD(2.0)],"derivedFrom":makeQuery(id+"F14.opExtrude","SWEPT_FACE",FACE,{"disambiguationData":[OSD([sQuery(id+"F13.wireOp",EDGE,"E10")])]})})],"blendedInto":[makeQuery(id+"F27.opBoolean","COPY",FACE,{"disambiguationData":[OD(2.0)],"derivedFrom":makeQuery(id+"F14.opExtrude","SWEPT_FACE",FACE,{"disambiguationData":[OSD([sQuery(id+"F13.wireOp",EDGE,"E10")])]})})]});
            fillet(context, id + "F30", {"entities" : qUnion([Q0]), "radius" : 1 * mm, "tangentPropagation" : true, "allowEdgeOverflow" : false});
        }
    });
